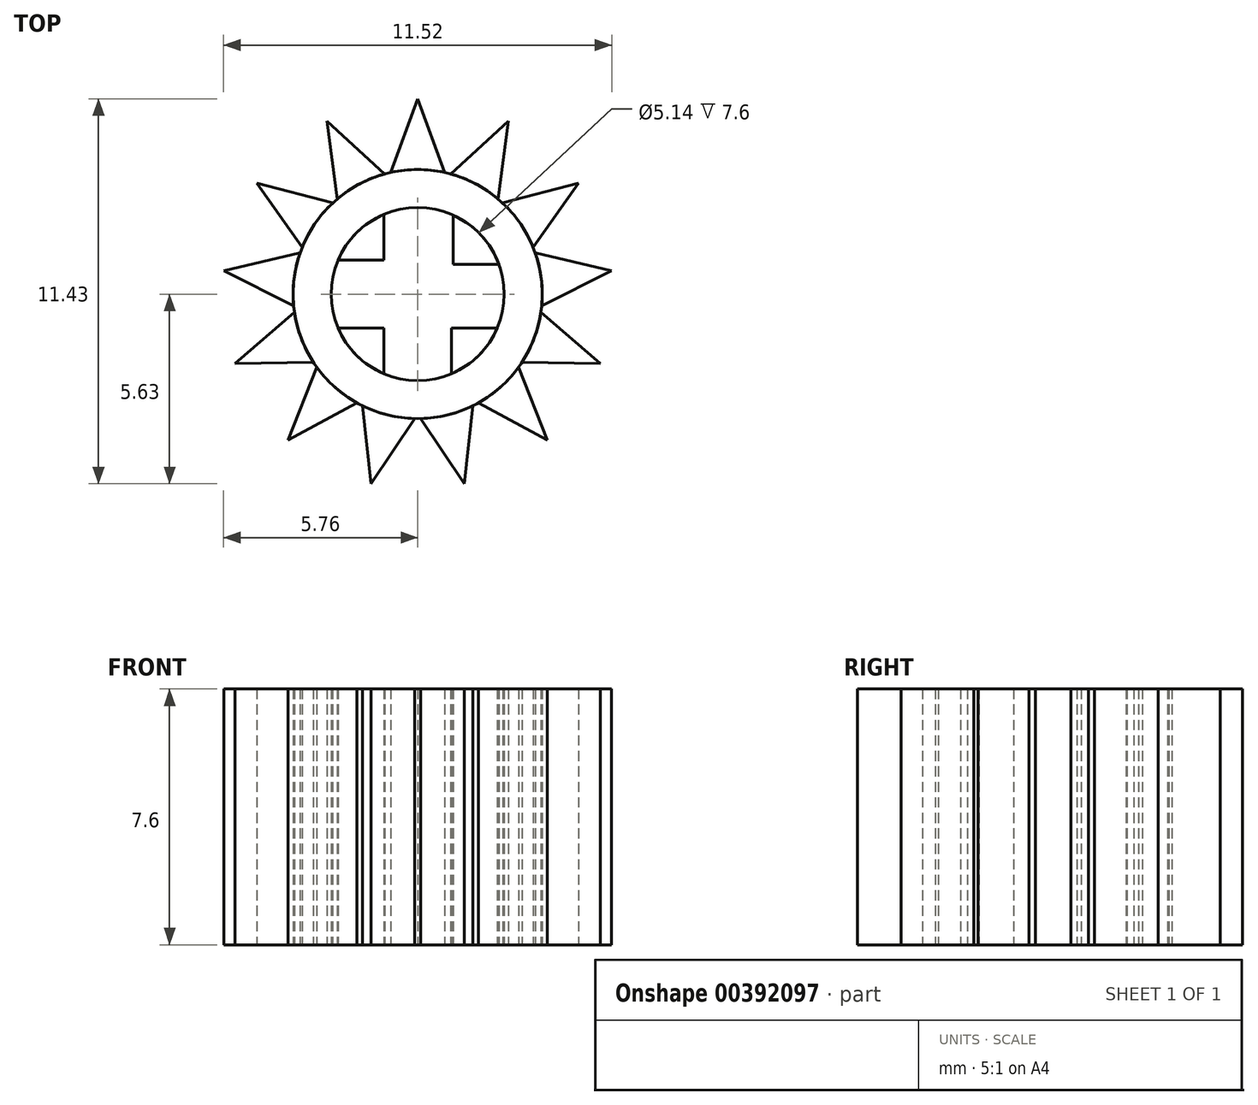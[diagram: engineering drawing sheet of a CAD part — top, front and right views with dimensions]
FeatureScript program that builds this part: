
annotation { "Feature Type Name" : "Feature", "Feature Type Description" : "" }
export const myFeature = defineFeature(function(context is Context, id is Id, definition is map)
    precondition{}
    {
        {
            var Q0;
            Q0=qCreatedBy(makeId("Top.planeOp"),FACE);
            var sketch = newSketch(context, id + "F0", { "sketchPlane" : qUnion([Q0])});
            skCircle(sketch, "E0", {"center": v(0, 0) * mm, "radius": 3.7 * mm});
            skLineSegment(sketch, "E1", {"start": v(0, 3.7) * mm, "end": v(0, 5.8) * mm});
            skLineSegment(sketch, "E2", {"start": v(0, 5.8) * mm, "end": v(-0.8, 3.61) * mm});
            skLineSegment(sketch, "E3", {"start": v(0, 5.8) * mm, "end": v(0.8, 3.61) * mm});
            skCircle(sketch, "E4", {"center": v(0, 0) * mm, "radius": 2.57 * mm});
            skLineSegment(sketch, "E5", {"start": v(1.05, 2.34) * mm, "end": v(1.05, 0.88) * mm});
            skLineSegment(sketch, "E6", {"start": v(1.05, 0.88) * mm, "end": v(2.41, 0.88) * mm});
            skLineSegment(sketch, "E7", {"start": v(2.37, -1) * mm, "end": v(1, -1) * mm});
            skLineSegment(sketch, "E8", {"start": v(1, -1) * mm, "end": v(1, -2.37) * mm});
            skLineSegment(sketch, "E9", {"start": v(-2.37, -1) * mm, "end": v(-1, -1) * mm});
            skLineSegment(sketch, "E10", {"start": v(-1, -1) * mm, "end": v(-1, -2.37) * mm});
            skLineSegment(sketch, "E11", {"start": v(-1, 2.37) * mm, "end": v(-1, 1) * mm});
            skLineSegment(sketch, "E12", {"start": v(-1, 1) * mm, "end": v(-2.37, 1) * mm});
            skSolve(sketch);
        }
        {
            var Q0;
            {var subQ0=sQuery(id+"F0.wireOp",EDGE,"E1");Q0=makeQuery(id+"F0.imprint","IMPRINT",FACE,{"disambiguationData":[TD([[makeQuery(id+"F0.imprint","IMPRINT",EDGE,{"derivedFrom":subQ0}),1.0]])]});}
            var Q1;
            {var subQ0=sQuery(id+"F0.wireOp",EDGE,"E1");Q1=makeQuery(id+"F0.imprint","IMPRINT",FACE,{"disambiguationData":[TD([[makeQuery(id+"F0.imprint","IMPRINT",EDGE,{"derivedFrom":subQ0}),-1.0]])]});}
            extrude(context, id + "F1", {"entities" : qUnion([Q0, Q1]), "depth" : 7.6 * mm});
        }
        {
            var Q0;
            Q0=qCreatedBy(makeId("Right.planeOp"),FACE);
            var sketch = newSketch(context, id + "F2", { "sketchPlane" : qUnion([Q0])});
            skLineSegment(sketch, "E13", {"start": v(0, 0) * mm, "end": v(0, 14.49) * mm});
            skSolve(sketch);
        }
        {
            var Q0;
            Q0=makeQuery(id+"F1.opExtrude","SWEPT_BODY",BODY,{"disambiguationData":[OSD([sQuery(id+"F0.wireOp",EDGE,"E0"),sQuery(id+"F0.wireOp",EDGE,"E2"),sQuery(id+"F0.wireOp",EDGE,"E3")])]});
            var Q1;
            Q1=sQuery(id+"F2.wireOp",EDGE,"E13");
            circularPattern(context, id + "F3", {"entities" : qUnion([Q0]), "axis" : qUnion([Q1]), "angle" : 360 * degree, "instanceCount" : 13, "equalSpace" : true});
        }
        {
            var Q0;
            {var subQ0=sQuery(id+"F0.wireOp",EDGE,"E11");Q0=makeQuery(id+"F0.imprint","IMPRINT",FACE,{"disambiguationData":[TD([[makeQuery(id+"F0.imprint","IMPRINT",EDGE,{"derivedFrom":subQ0}),-1.0]])]});}
            var Q1;
            {var subQ0=sQuery(id+"F0.wireOp",EDGE,"E5");Q1=makeQuery(id+"F0.imprint","IMPRINT",FACE,{"disambiguationData":[TD([[makeQuery(id+"F0.imprint","IMPRINT",EDGE,{"derivedFrom":subQ0}),1.0]])]});}
            var Q2;
            {var subQ0=sQuery(id+"F0.wireOp",EDGE,"E7");Q2=makeQuery(id+"F0.imprint","IMPRINT",FACE,{"disambiguationData":[TD([[makeQuery(id+"F0.imprint","IMPRINT",EDGE,{"derivedFrom":subQ0}),1.0]])]});}
            var Q3;
            {var subQ0=sQuery(id+"F0.wireOp",EDGE,"E9");Q3=makeQuery(id+"F0.imprint","IMPRINT",FACE,{"disambiguationData":[TD([[makeQuery(id+"F0.imprint","IMPRINT",EDGE,{"derivedFrom":subQ0}),-1.0]])]});}
            extrude(context, id + "F4", {"entities" : qUnion([Q0, Q1, Q2, Q3]), "depth" : 7.6 * mm});
        }
        {
            var Q0;
            {var subQ7=sQuery(id+"F0.wireOp",EDGE,"E0");var subQ8=makeQuery(id+"F0.imprint","INTERSECT",VERTEX,{"derivedFrom":[subQ7,sQuery(id+"F0.wireOp",EDGE,"E1")]});Q0=makeQuery(id+"F0.imprint","IMPRINT",FACE,{"disambiguationData":[TD([[makeQuery(id+"F0.imprint","IMPRINT",EDGE,{"disambiguationData":[TD([[subQ8,1.0]])],"derivedFrom":subQ7}),1.0]])]});}
            extrude(context, id + "F5", {"entities" : qUnion([Q0]), "depth" : 7.6 * mm});
        }
    });
